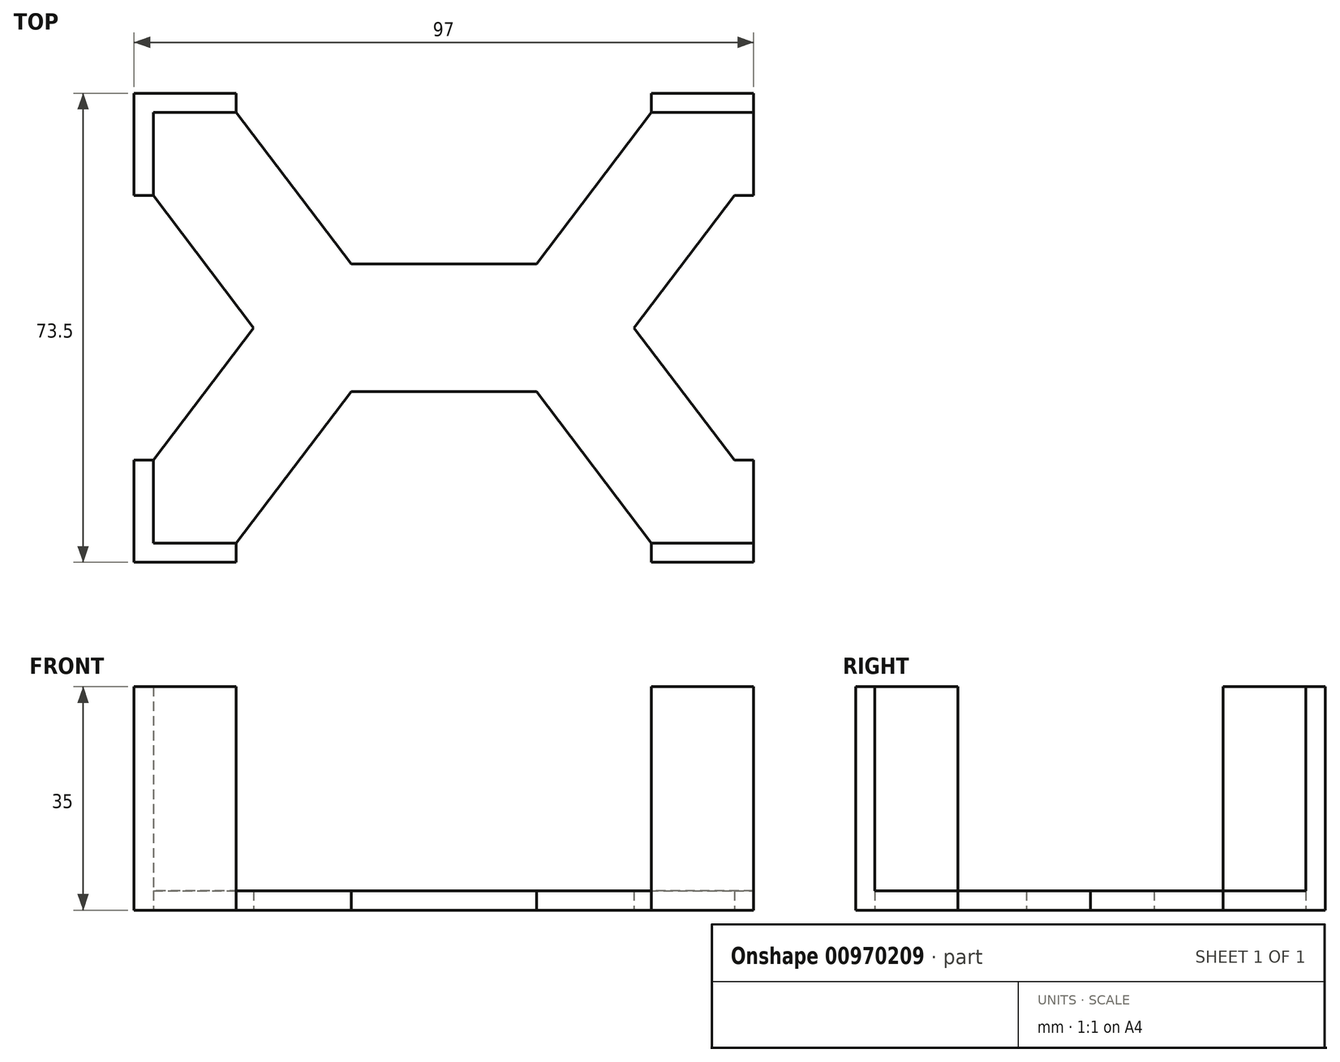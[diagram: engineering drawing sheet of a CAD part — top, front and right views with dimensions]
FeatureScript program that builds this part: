
annotation { "Feature Type Name" : "Feature", "Feature Type Description" : "" }
export const myFeature = defineFeature(function(context is Context, id is Id, definition is map)
    precondition{}
    {
        {
            var Q0;
            Q0=qCreatedBy(makeId("Top.planeOp"),FACE);
            var sketch = newSketch(context, id + "F0", { "sketchPlane" : qUnion([Q0])});
            skLineSegment(sketch, "E0.bottom", {"start": v(27.5, 10) * mm, "end": v(-27.5, 10) * mm});
            skLineSegment(sketch, "E0.top", {"start": v(27.5, -10) * mm, "end": v(-27.5, -10) * mm});
            skLineSegment(sketch, "E0.left", {"start": v(27.5, 10) * mm, "end": v(27.5, -10) * mm});
            skLineSegment(sketch, "E0.right", {"start": v(-27.5, 10) * mm, "end": v(-27.5, -10) * mm});
            skPoint(sketch, "E0.middle", {"position": v(0, 0) * mm});
            skLineSegment(sketch, "E1.bottom", {"start": v(45.5, 20.75) * mm, "end": v(32.5, 20.75) * mm});
            skLineSegment(sketch, "E1.top", {"start": v(45.5, 33.75) * mm, "end": v(32.5, 33.75) * mm});
            skLineSegment(sketch, "E1.left", {"start": v(45.5, 20.75) * mm, "end": v(45.5, 33.75) * mm});
            skLineSegment(sketch, "E1.right", {"start": v(32.5, 20.75) * mm, "end": v(32.5, 33.75) * mm});
            skPoint(sketch, "E1.middle", {"position": v(39, 27.25) * mm});
            skLineSegment(sketch, "E2", {"start": v(32.5, 33.75) * mm, "end": v(32.5, 36.75) * mm});
            skLineSegment(sketch, "E3", {"start": v(32.5, 36.75) * mm, "end": v(45.5, 36.75) * mm});
            skLineSegment(sketch, "E4", {"start": v(45.5, 36.75) * mm, "end": v(45.5, 33.75) * mm});
            skLineSegment(sketch, "E5", {"start": v(45.5, 20.75) * mm, "end": v(48.5, 20.75) * mm});
            skLineSegment(sketch, "E6", {"start": v(48.5, 20.75) * mm, "end": v(48.5, 33.75) * mm});
            skLineSegment(sketch, "E7", {"start": v(48.5, 33.75) * mm, "end": v(45.5, 33.75) * mm});
            skLineSegment(sketch, "E8", {"start": v(45.5, 36.75) * mm, "end": v(48.5, 36.75) * mm});
            skLineSegment(sketch, "E9", {"start": v(48.5, 36.75) * mm, "end": v(48.5, 33.75) * mm});
            skLineSegment(sketch, "E10", {"start": v(14.5, 10) * mm, "end": v(14.5, -3) * mm});
            skLineSegment(sketch, "E11", {"start": v(14.5, -3) * mm, "end": v(27.5, -3) * mm});
            skLineSegment(sketch, "E12", {"start": v(14.5, 10) * mm, "end": v(32.5, 33.75) * mm});
            skLineSegment(sketch, "E13", {"start": v(27.5, -3) * mm, "end": v(45.5, 20.75) * mm});
            skLineSegment(sketch, "E14.MirrorCS", {"start": v(-45.5, 36.75) * mm, "end": v(-45.5, 33.75) * mm});
            skLineSegment(sketch, "E15.MirrorCS", {"start": v(-48.5, 33.75) * mm, "end": v(-45.5, 33.75) * mm});
            skLineSegment(sketch, "E16.MirrorCS", {"start": v(-48.5, 36.75) * mm, "end": v(-48.5, 33.75) * mm});
            skLineSegment(sketch, "E17.MirrorCS", {"start": v(-45.5, 36.75) * mm, "end": v(-48.5, 36.75) * mm});
            skLineSegment(sketch, "E18.MirrorCS", {"start": v(-32.5, 33.75) * mm, "end": v(-32.5, 36.75) * mm});
            skLineSegment(sketch, "E19.MirrorCS", {"start": v(-45.5, 20.75) * mm, "end": v(-48.5, 20.75) * mm});
            skLineSegment(sketch, "E20.MirrorCS", {"start": v(-45.5, 20.75) * mm, "end": v(-32.5, 20.75) * mm});
            skLineSegment(sketch, "E21.MirrorCS", {"start": v(-45.5, 33.75) * mm, "end": v(-32.5, 33.75) * mm});
            skLineSegment(sketch, "E22.MirrorCS", {"start": v(-32.5, 36.75) * mm, "end": v(-45.5, 36.75) * mm});
            skLineSegment(sketch, "E23.MirrorCS", {"start": v(-45.5, 20.75) * mm, "end": v(-45.5, 33.75) * mm});
            skPoint(sketch, "E24.MirrorP", {"position": v(-39, 27.25) * mm});
            skLineSegment(sketch, "E25.MirrorCS", {"start": v(-48.5, 20.75) * mm, "end": v(-48.5, 33.75) * mm});
            skLineSegment(sketch, "E26.MirrorCS", {"start": v(-32.5, 20.75) * mm, "end": v(-32.5, 33.75) * mm});
            skLineSegment(sketch, "E27.MirrorCS", {"start": v(-27.5, -3) * mm, "end": v(-45.5, 20.75) * mm});
            skLineSegment(sketch, "E28.MirrorCS", {"start": v(-14.5, -3) * mm, "end": v(-27.5, -3) * mm});
            skLineSegment(sketch, "E29.MirrorCS", {"start": v(-14.5, 10) * mm, "end": v(-32.5, 33.75) * mm});
            skLineSegment(sketch, "E30.MirrorCS", {"start": v(-14.5, 10) * mm, "end": v(-14.5, -3) * mm});
            skLineSegment(sketch, "E31.MirrorCS", {"start": v(45.5, -36.75) * mm, "end": v(45.5, -33.75) * mm});
            skLineSegment(sketch, "E32.MirrorCS", {"start": v(48.5, -33.75) * mm, "end": v(45.5, -33.75) * mm});
            skLineSegment(sketch, "E33.MirrorCS", {"start": v(-45.5, -36.75) * mm, "end": v(-45.5, -33.75) * mm});
            skLineSegment(sketch, "E34.MirrorCS", {"start": v(-48.5, -33.75) * mm, "end": v(-45.5, -33.75) * mm});
            skLineSegment(sketch, "E35.MirrorCS", {"start": v(45.5, -20.75) * mm, "end": v(48.5, -20.75) * mm});
            skLineSegment(sketch, "E36.MirrorCS", {"start": v(45.5, -36.75) * mm, "end": v(48.5, -36.75) * mm});
            skLineSegment(sketch, "E37.MirrorCS", {"start": v(48.5, -36.75) * mm, "end": v(48.5, -33.75) * mm});
            skLineSegment(sketch, "E38.MirrorCS", {"start": v(32.5, -33.75) * mm, "end": v(32.5, -36.75) * mm});
            skLineSegment(sketch, "E39.MirrorCS", {"start": v(-32.5, -33.75) * mm, "end": v(-32.5, -36.75) * mm});
            skLineSegment(sketch, "E40.MirrorCS", {"start": v(-45.5, -36.75) * mm, "end": v(-48.5, -36.75) * mm});
            skLineSegment(sketch, "E41.MirrorCS", {"start": v(-48.5, -36.75) * mm, "end": v(-48.5, -33.75) * mm});
            skLineSegment(sketch, "E42.MirrorCS", {"start": v(-45.5, -20.75) * mm, "end": v(-48.5, -20.75) * mm});
            skLineSegment(sketch, "E43.MirrorCS", {"start": v(48.5, -20.75) * mm, "end": v(48.5, -33.75) * mm});
            skLineSegment(sketch, "E44.MirrorCS", {"start": v(14.5, -10) * mm, "end": v(14.5, 3) * mm});
            skLineSegment(sketch, "E45.MirrorCS", {"start": v(-27.5, 3) * mm, "end": v(-45.5, -20.75) * mm});
            skLineSegment(sketch, "E46.MirrorCS", {"start": v(14.5, 3) * mm, "end": v(27.5, 3) * mm});
            skLineSegment(sketch, "E47.MirrorCS", {"start": v(-14.5, 3) * mm, "end": v(-27.5, 3) * mm});
            skLineSegment(sketch, "E48.MirrorCS", {"start": v(32.5, -36.75) * mm, "end": v(45.5, -36.75) * mm});
            skLineSegment(sketch, "E49.MirrorCS", {"start": v(14.5, -10) * mm, "end": v(32.5, -33.75) * mm});
            skLineSegment(sketch, "E50.MirrorCS", {"start": v(-14.5, -10) * mm, "end": v(-32.5, -33.75) * mm});
            skLineSegment(sketch, "E51.MirrorCS", {"start": v(27.5, 3) * mm, "end": v(45.5, -20.75) * mm});
            skLineSegment(sketch, "E52.MirrorCS", {"start": v(-32.5, -20.75) * mm, "end": v(-32.5, -33.75) * mm});
            skLineSegment(sketch, "E53.MirrorCS", {"start": v(-14.5, -10) * mm, "end": v(-14.5, 3) * mm});
            skLineSegment(sketch, "E54.MirrorCS", {"start": v(32.5, -20.75) * mm, "end": v(32.5, -33.75) * mm});
            skLineSegment(sketch, "E55.MirrorCS", {"start": v(45.5, -20.75) * mm, "end": v(32.5, -20.75) * mm});
            skPoint(sketch, "E56.MirrorP", {"position": v(-39, -27.25) * mm});
            skPoint(sketch, "E57.MirrorP", {"position": v(39, -27.25) * mm});
            skLineSegment(sketch, "E58.MirrorCS", {"start": v(45.5, -33.75) * mm, "end": v(32.5, -33.75) * mm});
            skLineSegment(sketch, "E59.MirrorCS", {"start": v(-45.5, -33.75) * mm, "end": v(-32.5, -33.75) * mm});
            skLineSegment(sketch, "E60.MirrorCS", {"start": v(-45.5, -20.75) * mm, "end": v(-45.5, -33.75) * mm});
            skLineSegment(sketch, "E61.MirrorCS", {"start": v(45.5, -20.75) * mm, "end": v(45.5, -33.75) * mm});
            skLineSegment(sketch, "E62.MirrorCS", {"start": v(-48.5, -20.75) * mm, "end": v(-48.5, -33.75) * mm});
            skLineSegment(sketch, "E63.MirrorCS", {"start": v(-32.5, -36.75) * mm, "end": v(-45.5, -36.75) * mm});
            skLineSegment(sketch, "E64.MirrorCS", {"start": v(-45.5, -20.75) * mm, "end": v(-32.5, -20.75) * mm});
            skSolve(sketch);
        }
        {
            var Q0;
            Q0=makeQuery(id+"F0.imprint","IMPRINT",FACE,{"disambiguationData":[TD([[makeQuery(id+"F0.imprint","IMPRINT",EDGE,{"derivedFrom":sQuery(id+"F0.wireOp",EDGE,"E20.MirrorCS")}),1.0]])]});
            var Q1;
            {var subQ6=sQuery(id+"F0.wireOp",EDGE,"E20.MirrorCS");Q1=makeQuery(id+"F0.imprint","IMPRINT",FACE,{"disambiguationData":[TD([[makeQuery(id+"F0.imprint","IMPRINT",EDGE,{"derivedFrom":subQ6}),-1.0]])]});}
            var Q2;
            {var subQ3=sQuery(id+"F0.wireOp",EDGE,"E30.MirrorCS");Q2=makeQuery(id+"F0.imprint","IMPRINT",FACE,{"disambiguationData":[TD([[makeQuery(id+"F0.imprint","IMPRINT",EDGE,{"derivedFrom":subQ3}),-1.0]])]});}
            var Q3;
            {var subQ0=sQuery(id+"F0.wireOp",EDGE,"E27.MirrorCS");var subQ3=sQuery(id+"F0.wireOp",EDGE,"E45.MirrorCS");var subQ5=makeQuery(id+"F0.imprint","INTERSECT",VERTEX,{"derivedFrom":[subQ0,subQ3]});Q3=makeQuery(id+"F0.imprint","IMPRINT",FACE,{"disambiguationData":[TD([[makeQuery(id+"F0.imprint","IMPRINT",EDGE,{"disambiguationData":[TD([[subQ5,1.0]])],"derivedFrom":subQ0}),-1.0]])]});}
            var Q4;
            {var subQ0=sQuery(id+"F0.wireOp",EDGE,"E28.MirrorCS");Q4=makeQuery(id+"F0.imprint","IMPRINT",FACE,{"disambiguationData":[TD([[makeQuery(id+"F0.imprint","IMPRINT",EDGE,{"derivedFrom":subQ0}),-1.0]])]});}
            var Q5;
            {var subQ3=sQuery(id+"F0.wireOp",EDGE,"E28.MirrorCS");Q5=makeQuery(id+"F0.imprint","IMPRINT",FACE,{"disambiguationData":[TD([[makeQuery(id+"F0.imprint","IMPRINT",EDGE,{"derivedFrom":subQ3}),1.0]])]});}
            var Q6;
            {var subQ0=sQuery(id+"F0.wireOp",EDGE,"E50.MirrorCS");Q6=makeQuery(id+"F0.imprint","IMPRINT",FACE,{"disambiguationData":[TD([[makeQuery(id+"F0.imprint","IMPRINT",EDGE,{"derivedFrom":subQ0}),-1.0]])]});}
            var Q7;
            Q7=makeQuery(id+"F0.imprint","IMPRINT",FACE,{"disambiguationData":[TD([[makeQuery(id+"F0.imprint","IMPRINT",EDGE,{"derivedFrom":sQuery(id+"F0.wireOp",EDGE,"E52.MirrorCS")}),-1.0]])]});
            var Q8;
            {var subQ5=sQuery(id+"F0.wireOp",EDGE,"E10");Q8=makeQuery(id+"F0.imprint","IMPRINT",FACE,{"disambiguationData":[TD([[makeQuery(id+"F0.imprint","IMPRINT",EDGE,{"derivedFrom":subQ5}),-1.0]])]});}
            var Q9;
            {var subQ3=sQuery(id+"F0.wireOp",EDGE,"E10");Q9=makeQuery(id+"F0.imprint","IMPRINT",FACE,{"disambiguationData":[TD([[makeQuery(id+"F0.imprint","IMPRINT",EDGE,{"derivedFrom":subQ3}),1.0]])]});}
            var Q10;
            {var subQ0=sQuery(id+"F0.wireOp",EDGE,"E11");Q10=makeQuery(id+"F0.imprint","IMPRINT",FACE,{"disambiguationData":[TD([[makeQuery(id+"F0.imprint","IMPRINT",EDGE,{"derivedFrom":subQ0}),1.0]])]});}
            var Q11;
            {var subQ3=sQuery(id+"F0.wireOp",EDGE,"E11");Q11=makeQuery(id+"F0.imprint","IMPRINT",FACE,{"disambiguationData":[TD([[makeQuery(id+"F0.imprint","IMPRINT",EDGE,{"derivedFrom":subQ3}),-1.0]])]});}
            var Q12;
            {var subQ0=sQuery(id+"F0.wireOp",EDGE,"E13");var subQ3=sQuery(id+"F0.wireOp",EDGE,"E51.MirrorCS");var subQ5=makeQuery(id+"F0.imprint","INTERSECT",VERTEX,{"derivedFrom":[subQ0,subQ3]});Q12=makeQuery(id+"F0.imprint","IMPRINT",FACE,{"disambiguationData":[TD([[makeQuery(id+"F0.imprint","IMPRINT",EDGE,{"disambiguationData":[TD([[subQ5,1.0]])],"derivedFrom":subQ0}),1.0]])]});}
            var Q13;
            {var subQ4=sQuery(id+"F0.wireOp",EDGE,"E49.MirrorCS");Q13=makeQuery(id+"F0.imprint","IMPRINT",FACE,{"disambiguationData":[TD([[makeQuery(id+"F0.imprint","IMPRINT",EDGE,{"derivedFrom":subQ4}),1.0]])]});}
            var Q14;
            {var subQ1=sQuery(id+"F0.wireOp",EDGE,"E1.bottom");Q14=makeQuery(id+"F0.imprint","IMPRINT",FACE,{"disambiguationData":[TD([[makeQuery(id+"F0.imprint","IMPRINT",EDGE,{"derivedFrom":subQ1}),1.0]])]});}
            var Q15;
            Q15=makeQuery(id+"F0.imprint","IMPRINT",FACE,{"disambiguationData":[TD([[makeQuery(id+"F0.imprint","IMPRINT",EDGE,{"derivedFrom":sQuery(id+"F0.wireOp",EDGE,"E54.MirrorCS")}),1.0]])]});
            var Q16;
            Q16=makeQuery(id+"F0.imprint","IMPRINT",FACE,{"disambiguationData":[TD([[makeQuery(id+"F0.imprint","IMPRINT",EDGE,{"derivedFrom":sQuery(id+"F0.wireOp",EDGE,"E32.MirrorCS")}),-1.0]])]});
            var Q17;
            Q17=makeQuery(id+"F0.imprint","IMPRINT",FACE,{"disambiguationData":[TD([[makeQuery(id+"F0.imprint","IMPRINT",EDGE,{"derivedFrom":sQuery(id+"F0.wireOp",EDGE,"E1.bottom")}),-1.0]])]});
            var Q18;
            Q18=makeQuery(id+"F0.imprint","IMPRINT",FACE,{"disambiguationData":[TD([[makeQuery(id+"F0.imprint","IMPRINT",EDGE,{"derivedFrom":sQuery(id+"F0.wireOp",EDGE,"E1.left")}),-1.0]])]});
            extrude(context, id + "F1", {"entities" : qUnion([Q0, Q1, Q2, Q3, Q4, Q5, Q6, Q7, Q8, Q9, Q10, Q11, Q12, Q13, Q14, Q15, Q16, Q17, Q18]), "depth" : 3 * mm, "offsetDistance" : 25 * mm});
        }
        {
            var Q0;
            Q0=makeQuery(id+"F0.imprint","IMPRINT",FACE,{"disambiguationData":[TD([[makeQuery(id+"F0.imprint","IMPRINT",EDGE,{"derivedFrom":sQuery(id+"F0.wireOp",EDGE,"E15.MirrorCS")}),-1.0]])]});
            var Q1;
            Q1=makeQuery(id+"F0.imprint","IMPRINT",FACE,{"disambiguationData":[TD([[makeQuery(id+"F0.imprint","IMPRINT",EDGE,{"derivedFrom":sQuery(id+"F0.wireOp",EDGE,"E14.MirrorCS")}),-1.0]])]});
            var Q2;
            Q2=makeQuery(id+"F0.imprint","IMPRINT",FACE,{"disambiguationData":[TD([[makeQuery(id+"F0.imprint","IMPRINT",EDGE,{"derivedFrom":sQuery(id+"F0.wireOp",EDGE,"E14.MirrorCS")}),1.0]])]});
            var Q3;
            Q3=makeQuery(id+"F0.imprint","IMPRINT",FACE,{"disambiguationData":[TD([[makeQuery(id+"F0.imprint","IMPRINT",EDGE,{"derivedFrom":sQuery(id+"F0.wireOp",EDGE,"E34.MirrorCS")}),1.0]])]});
            var Q4;
            Q4=makeQuery(id+"F0.imprint","IMPRINT",FACE,{"disambiguationData":[TD([[makeQuery(id+"F0.imprint","IMPRINT",EDGE,{"derivedFrom":sQuery(id+"F0.wireOp",EDGE,"E33.MirrorCS")}),1.0]])]});
            var Q5;
            Q5=makeQuery(id+"F0.imprint","IMPRINT",FACE,{"disambiguationData":[TD([[makeQuery(id+"F0.imprint","IMPRINT",EDGE,{"derivedFrom":sQuery(id+"F0.wireOp",EDGE,"E33.MirrorCS")}),-1.0]])]});
            var Q6;
            Q6=makeQuery(id+"F0.imprint","IMPRINT",FACE,{"disambiguationData":[TD([[makeQuery(id+"F0.imprint","IMPRINT",EDGE,{"derivedFrom":sQuery(id+"F0.wireOp",EDGE,"E31.MirrorCS")}),1.0]])]});
            var Q7;
            Q7=makeQuery(id+"F0.imprint","IMPRINT",FACE,{"disambiguationData":[TD([[makeQuery(id+"F0.imprint","IMPRINT",EDGE,{"derivedFrom":sQuery(id+"F0.wireOp",EDGE,"E31.MirrorCS")}),-1.0]])]});
            var Q8;
            Q8=makeQuery(id+"F0.imprint","IMPRINT",FACE,{"disambiguationData":[TD([[makeQuery(id+"F0.imprint","IMPRINT",EDGE,{"derivedFrom":sQuery(id+"F0.wireOp",EDGE,"E1.top")}),-1.0]])]});
            var Q9;
            Q9=makeQuery(id+"F0.imprint","IMPRINT",FACE,{"disambiguationData":[TD([[makeQuery(id+"F0.imprint","IMPRINT",EDGE,{"derivedFrom":sQuery(id+"F0.wireOp",EDGE,"E4")}),1.0]])]});
            extrude(context, id + "F2", {"entities" : qUnion([Q0, Q1, Q2, Q3, Q4, Q5, Q6, Q7, Q8, Q9]), "operationType" : NewBodyOperationType.ADD, "depth" : 35 * mm, "offsetDistance" : 25 * mm});
        }
    });
